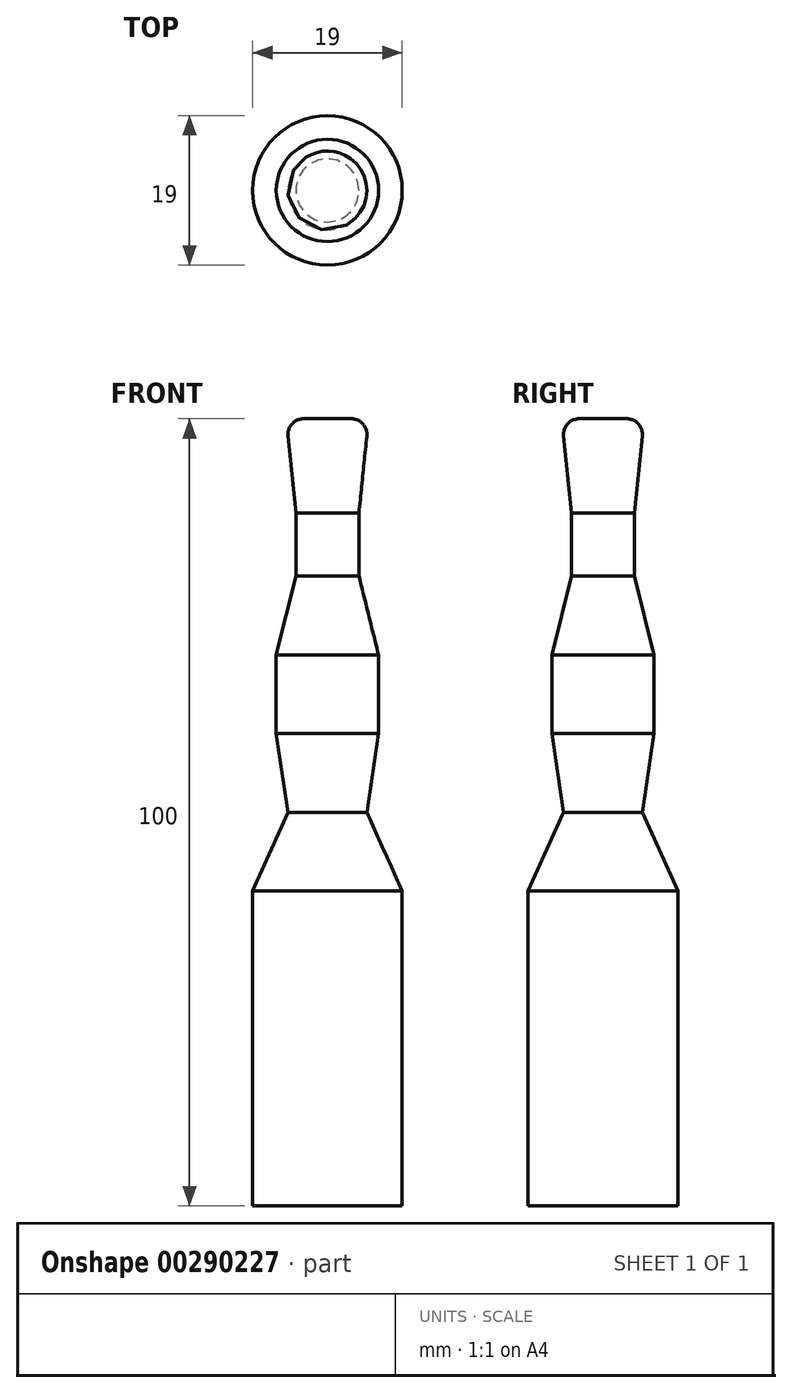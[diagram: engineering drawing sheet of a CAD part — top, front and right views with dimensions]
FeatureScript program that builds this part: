
annotation { "Feature Type Name" : "Feature", "Feature Type Description" : "" }
export const myFeature = defineFeature(function(context is Context, id is Id, definition is map)
    precondition{}
    {
        {
            var Q0;
            Q0=qCreatedBy(makeId("Front.planeOp"),FACE);
            var sketch = newSketch(context, id + "F0", { "sketchPlane" : qUnion([Q0])});
            skLineSegment(sketch, "E0", {"start": v(0, 0) * mm, "end": v(3.01, 0) * mm});
            skLineSegment(sketch, "E1", {"start": v(0, 0) * mm, "end": v(0, -100) * mm});
            skArc(sketch, "E2", {"start": v(5, -2.2) * mm, "mid": v(4.5, -0.66) * mm, "end": v(3.01, 0) * mm});
            skLineSegment(sketch, "E3", {"start": v(5, -2.2) * mm, "end": v(4, -12) * mm});
            skLineSegment(sketch, "E4", {"start": v(4, -12) * mm, "end": v(4, -20) * mm});
            skLineSegment(sketch, "E5", {"start": v(4, -20) * mm, "end": v(6.5, -30) * mm});
            skLineSegment(sketch, "E6", {"start": v(6.5, -30) * mm, "end": v(6.5, -40) * mm});
            skLineSegment(sketch, "E7", {"start": v(6.5, -40) * mm, "end": v(5, -50) * mm});
            skLineSegment(sketch, "E8", {"start": v(5, -50) * mm, "end": v(9.5, -60) * mm});
            skLineSegment(sketch, "E9", {"start": v(9.5, -60) * mm, "end": v(9.5, -100) * mm});
            skLineSegment(sketch, "E10", {"start": v(9.5, -100) * mm, "end": v(0, -100) * mm});
            skSolve(sketch);
        }
        {
            var Q0;
            Q0 = qSketchRegion(id + "F0", true);
            var Q1;
            Q1=sQuery(id+"F0.wireOp",EDGE,"E1");
            revolve(context, id + "F1", {"entities" : qUnion([Q0]), "axis" : qUnion([Q1]), "revolveType" : RevolveType.FULL});
        }
    });
